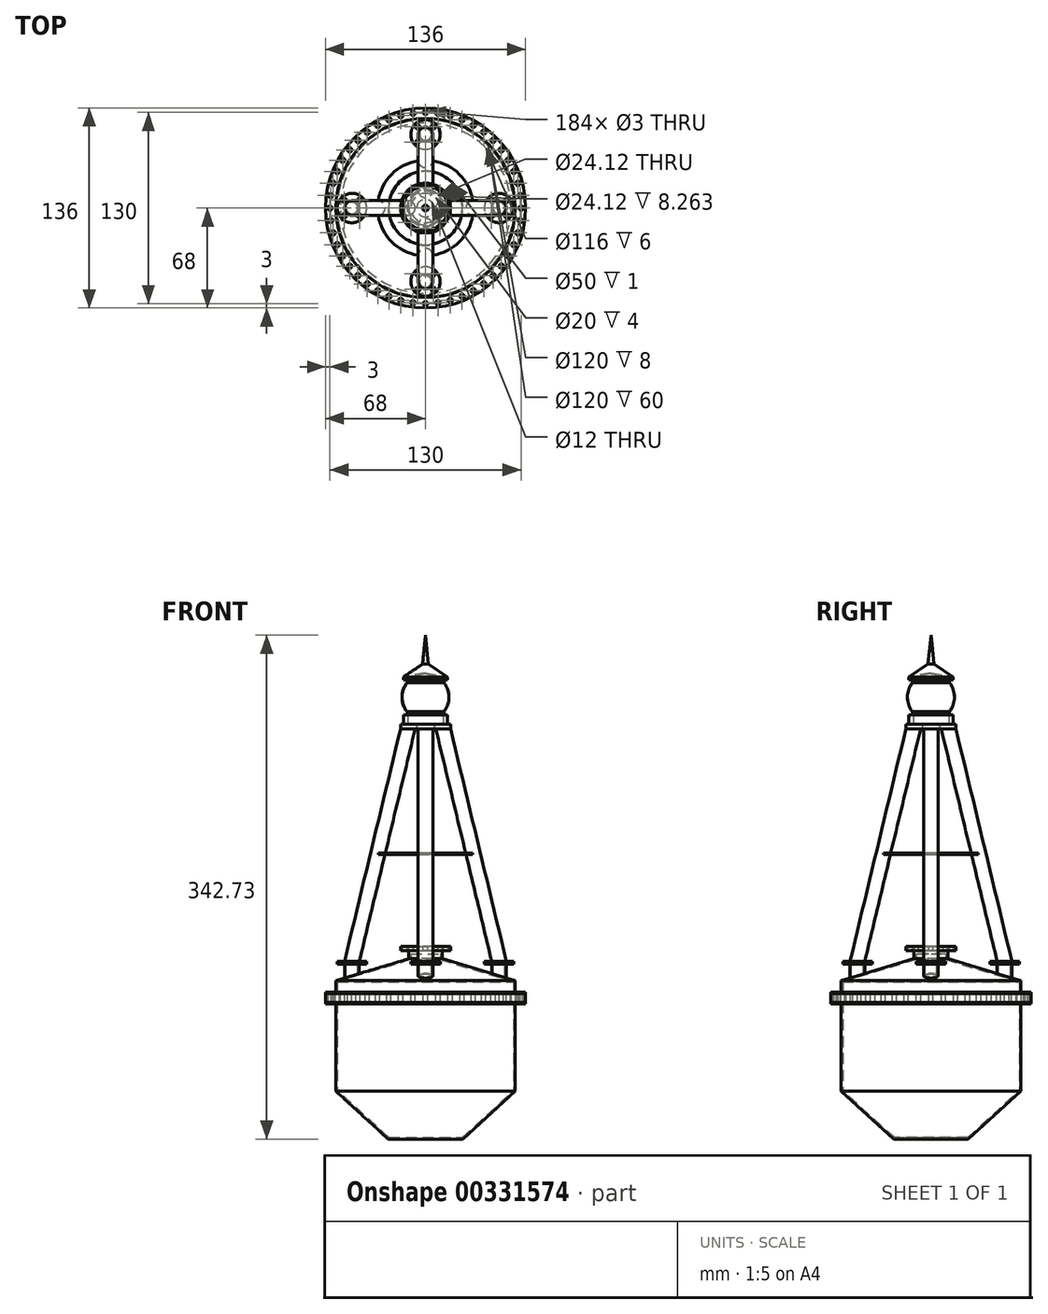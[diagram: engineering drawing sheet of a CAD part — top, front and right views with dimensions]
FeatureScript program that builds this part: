
annotation { "Feature Type Name" : "Feature", "Feature Type Description" : "" }
export const myFeature = defineFeature(function(context is Context, id is Id, definition is map)
    precondition{}
    {
        {
            var Q0;
            Q0=qCreatedBy(makeId("Front.planeOp"),FACE);
            var sketch = newSketch(context, id + "F0", { "sketchPlane" : qUnion([Q0])});
            skLineSegment(sketch, "E0", {"start": v(10, 50) * mm, "end": v(10, 43) * mm});
            skLineSegment(sketch, "E1", {"start": v(10, 43) * mm, "end": v(60, 28) * mm});
            skLineSegment(sketch, "E2", {"start": v(60, 28) * mm, "end": v(60, 20) * mm});
            skLineSegment(sketch, "E3", {"start": v(60, 20) * mm, "end": v(68, 20) * mm});
            skLineSegment(sketch, "E4", {"start": v(68, 14) * mm, "end": v(60, 14) * mm});
            skLineSegment(sketch, "E5", {"start": v(60, 14) * mm, "end": v(60, -46) * mm});
            skLineSegment(sketch, "E6", {"start": v(60, -46) * mm, "end": v(25, -78) * mm});
            skLineSegment(sketch, "E7", {"start": v(25, -78) * mm, "end": v(0, -78) * mm});
            skLineSegment(sketch, "E8.0", {"start": v(61, 21) * mm, "end": v(68, 21) * mm});
            skLineSegment(sketch, "E8.1", {"start": v(17, 49) * mm, "end": v(11.5, 49) * mm});
            skLineSegment(sketch, "E8.2", {"start": v(11.5, 49) * mm, "end": v(11.5, 43.6) * mm});
            skLineSegment(sketch, "E8.3", {"start": v(11.5, 43.6) * mm, "end": v(61, 28.74) * mm});
            skLineSegment(sketch, "E8.4", {"start": v(61, 28.74) * mm, "end": v(61, 21) * mm});
            skLineSegment(sketch, "E9.0", {"start": v(25.39, -79) * mm, "end": v(0, -79) * mm});
            skLineSegment(sketch, "E9.1", {"start": v(61, -46.44) * mm, "end": v(25.39, -79) * mm});
            skLineSegment(sketch, "E9.2", {"start": v(61, 13) * mm, "end": v(61, -46.44) * mm});
            skLineSegment(sketch, "E9.3", {"start": v(68, 13) * mm, "end": v(61, 13) * mm});
            skLineSegment(sketch, "E10", {"start": v(68, 21) * mm, "end": v(68, 20) * mm});
            skLineSegment(sketch, "E11", {"start": v(68, 14) * mm, "end": v(68, 13) * mm});
            skLineSegment(sketch, "E12", {"start": v(0, -78) * mm, "end": v(0, -79) * mm});
            skLineSegment(sketch, "E13.top", {"start": v(60, 14) * mm, "end": v(68, 14) * mm});
            skLineSegment(sketch, "E14", {"start": v(10, 50) * mm, "end": v(17, 50) * mm});
            skLineSegment(sketch, "E15", {"start": v(17, 50) * mm, "end": v(17, 49) * mm});
            skLineSegment(sketch, "E16", {"start": v(0, 0) * mm, "end": v(0, 63.77) * mm, "construction": true});
            skSolve(sketch);
        }
        {
            var Q0;
            Q0=makeQuery(id+"F0.imprint","IMPRINT",FACE,{"disambiguationData":[TD([[makeQuery(id+"F0.imprint","IMPRINT",EDGE,{"derivedFrom":sQuery(id+"F0.wireOp",EDGE,"E0")}),1.0]])]});
            var Q1;
            Q1=makeQuery(id+"F0.imprint","IMPRINT",FACE,{"disambiguationData":[TD([[makeQuery(id+"F0.imprint","IMPRINT",EDGE,{"derivedFrom":sQuery(id+"F0.wireOp",EDGE,"E5")}),1.0]])]});
            var Q2;
            Q2=sQuery(id+"F0.wireOp",EDGE,"E16");
            revolve(context, id + "F1", {"entities" : qUnion([Q0, Q1]), "axis" : qUnion([Q2]), "revolveType" : RevolveType.FULL});
        }
        {
            var Q0;
            Q0=qCreatedBy(makeId("Front.planeOp"),FACE);
            var sketch = newSketch(context, id + "F2", { "sketchPlane" : qUnion([Q0])});
            skLineSegment(sketch, "E17.0", {"start": v(58, 20) * mm, "end": v(68, 20) * mm});
            skLineSegment(sketch, "E17.1", {"start": v(58, 14) * mm, "end": v(68, 14) * mm});
            skLineSegment(sketch, "E18", {"start": v(68, 20) * mm, "end": v(68, 14) * mm});
            skLineSegment(sketch, "E19", {"start": v(58, 20) * mm, "end": v(58, 14) * mm});
            skPoint(sketch, "E20.orphan", {"position": v(-68, 20) * mm});
            skPoint(sketch, "E21.orphan", {"position": v(-68, 14) * mm});
            skLineSegment(sketch, "E22", {"start": v(0, 35.56) * mm, "end": v(0, -17.02) * mm, "construction": true});
            skSolve(sketch);
        }
        {
            var Q0;
            Q0 = qSketchRegion(id + "F2", true);
            var Q1;
            Q1=sQuery(id+"F2.wireOp",EDGE,"E22");
            revolve(context, id + "F3", {"entities" : qUnion([Q0]), "axis" : qUnion([Q1]), "revolveType" : RevolveType.FULL});
        }
        {
            var Q0;
            Q0=makeQuery(id+"F1.opRevolve","SWEPT_FACE",FACE,{"disambiguationData":[OSD([sQuery(id+"F0.wireOp",EDGE,"E14")])]});
            var sketch = newSketch(context, id + "F4", { "sketchPlane" : qUnion([Q0])});
            skCircle(sketch, "E23.0", {"center": v(0, 0) * mm, "radius": 10 * mm});
            skSolve(sketch);
        }
        {
            var Q0;
            Q0 = qSketchRegion(id + "F4", true);
            extrude(context, id + "F5", {"entities" : qUnion([Q0]), "oppositeDirection" : true, "depth" : 3 * mm});
        }
        {
            var Q0;
            Q0=makeQuery(id+"F5.opExtrude","CAP_FACE",FACE,{"disambiguationData":[OSD([sQuery(id+"F4.wireOp",EDGE,"E23.0")])],"isStart":true});
            var sketch = newSketch(context, id + "F6", { "sketchPlane" : qUnion([Q0])});
            skCircle(sketch, "E24.0", {"center": v(0, 0) * mm, "radius": 17 * mm});
            skSolve(sketch);
        }
        {
            var Q0;
            Q0 = qSketchRegion(id + "F6", true);
            extrude(context, id + "F7", {"entities" : qUnion([Q0]), "operationType" : NewBodyOperationType.ADD, "depth" : 2 * mm});
        }
        {
            var Q0;
            Q0=makeQuery(id+"F7.opExtrude","CAP_FACE",FACE,{"disambiguationData":[OSD([sQuery(id+"F6.wireOp",EDGE,"E24.0")])],"isStart":false});
            var sketch = newSketch(context, id + "F8", { "sketchPlane" : qUnion([Q0])});
            skCircle(sketch, "E25", {"center": v(0, 0) * mm, "radius": 14 * mm, "construction": true});
            skCircle(sketch, "E26", {"center": v(0, 14) * mm, "radius": 1.5 * mm});
            skCircle(sketch, "E27.1.0", {"center": v(-9.9, 9.9) * mm, "radius": 1.5 * mm});
            skCircle(sketch, "E27.2.0", {"center": v(-14, 0) * mm, "radius": 1.5 * mm});
            skCircle(sketch, "E27.3.0", {"center": v(-9.9, -9.9) * mm, "radius": 1.5 * mm});
            skCircle(sketch, "E27.4.0", {"center": v(0, -14) * mm, "radius": 1.5 * mm});
            skCircle(sketch, "E27.5.0", {"center": v(9.9, -9.9) * mm, "radius": 1.5 * mm});
            skCircle(sketch, "E27.6.0", {"center": v(14, 0) * mm, "radius": 1.5 * mm});
            skCircle(sketch, "E27.7.0", {"center": v(9.9, 9.9) * mm, "radius": 1.5 * mm});
            skLineSegment(sketch, "E28", {"start": v(-9.9, 9.9) * mm, "end": v(0, 0) * mm, "construction": true});
            skSolve(sketch);
        }
        {
            var Q0;
            Q0 = qSketchRegion(id + "F8", true);
            var Q1;
            Q1=makeQuery(id+"F1.opRevolve","SWEPT_FACE",FACE,{"disambiguationData":[OSD([sQuery(id+"F0.wireOp",EDGE,"E8.1")])]});
            extrude(context, id + "F9", {"entities" : qUnion([Q0]), "operationType" : NewBodyOperationType.REMOVE, "endBound" : BoundingType.UP_TO_SURFACE, "oppositeDirection" : true, "endBoundEntityFace" : qUnion([Q1]), "depth" : 25 * mm});
        }
        {
            var Q0;
            Q0=makeQuery(id+"F1.opRevolve","SWEPT_FACE",FACE,{"disambiguationData":[OSD([sQuery(id+"F0.wireOp",EDGE,"E8.0")])]});
            var sketch = newSketch(context, id + "F10", { "sketchPlane" : qUnion([Q0])});
            skCircle(sketch, "E29", {"center": v(0, 0) * mm, "radius": 65 * mm, "construction": true});
            skCircle(sketch, "E30", {"center": v(-65, 0) * mm, "radius": 1.5 * mm});
            skCircle(sketch, "E31.1.0", {"center": v(-64.44, -8.48) * mm, "radius": 1.5 * mm});
            skCircle(sketch, "E31.2.0", {"center": v(-62.79, -16.82) * mm, "radius": 1.5 * mm});
            skCircle(sketch, "E31.3.0", {"center": v(-60.05, -24.87) * mm, "radius": 1.5 * mm});
            skCircle(sketch, "E31.4.0", {"center": v(-56.3, -32.5) * mm, "radius": 1.5 * mm});
            skCircle(sketch, "E31.5.0", {"center": v(-51.57, -39.57) * mm, "radius": 1.5 * mm});
            skCircle(sketch, "E31.6.0", {"center": v(-45.96, -45.96) * mm, "radius": 1.5 * mm});
            skCircle(sketch, "E31.7.0", {"center": v(-39.57, -51.57) * mm, "radius": 1.5 * mm});
            skCircle(sketch, "E31.8.0", {"center": v(-32.5, -56.3) * mm, "radius": 1.5 * mm});
            skCircle(sketch, "E31.9.0", {"center": v(-24.87, -60.05) * mm, "radius": 1.5 * mm});
            skCircle(sketch, "E31.10.0", {"center": v(-16.82, -62.79) * mm, "radius": 1.5 * mm});
            skCircle(sketch, "E31.11.0", {"center": v(-8.48, -64.44) * mm, "radius": 1.5 * mm});
            skCircle(sketch, "E31.12.0", {"center": v(0, -65) * mm, "radius": 1.5 * mm});
            skCircle(sketch, "E31.13.0", {"center": v(8.48, -64.44) * mm, "radius": 1.5 * mm});
            skCircle(sketch, "E31.14.0", {"center": v(16.82, -62.79) * mm, "radius": 1.5 * mm});
            skCircle(sketch, "E31.15.0", {"center": v(24.87, -60.05) * mm, "radius": 1.5 * mm});
            skCircle(sketch, "E31.16.0", {"center": v(32.5, -56.3) * mm, "radius": 1.5 * mm});
            skCircle(sketch, "E31.17.0", {"center": v(39.57, -51.57) * mm, "radius": 1.5 * mm});
            skCircle(sketch, "E31.18.0", {"center": v(45.96, -45.96) * mm, "radius": 1.5 * mm});
            skCircle(sketch, "E31.19.0", {"center": v(51.57, -39.57) * mm, "radius": 1.5 * mm});
            skCircle(sketch, "E31.20.0", {"center": v(56.3, -32.5) * mm, "radius": 1.5 * mm});
            skCircle(sketch, "E31.21.0", {"center": v(60.05, -24.87) * mm, "radius": 1.5 * mm});
            skCircle(sketch, "E31.22.0", {"center": v(62.79, -16.82) * mm, "radius": 1.5 * mm});
            skCircle(sketch, "E31.23.0", {"center": v(64.44, -8.48) * mm, "radius": 1.5 * mm});
            skCircle(sketch, "E31.24.0", {"center": v(65, 0) * mm, "radius": 1.5 * mm});
            skCircle(sketch, "E31.25.0", {"center": v(64.44, 8.48) * mm, "radius": 1.5 * mm});
            skCircle(sketch, "E31.26.0", {"center": v(62.79, 16.82) * mm, "radius": 1.5 * mm});
            skCircle(sketch, "E31.27.0", {"center": v(60.05, 24.87) * mm, "radius": 1.5 * mm});
            skCircle(sketch, "E31.28.0", {"center": v(56.3, 32.5) * mm, "radius": 1.5 * mm});
            skCircle(sketch, "E31.29.0", {"center": v(51.57, 39.57) * mm, "radius": 1.5 * mm});
            skCircle(sketch, "E31.30.0", {"center": v(45.96, 45.96) * mm, "radius": 1.5 * mm});
            skCircle(sketch, "E31.31.0", {"center": v(39.57, 51.57) * mm, "radius": 1.5 * mm});
            skCircle(sketch, "E31.32.0", {"center": v(32.5, 56.3) * mm, "radius": 1.5 * mm});
            skCircle(sketch, "E31.33.0", {"center": v(24.87, 60.05) * mm, "radius": 1.5 * mm});
            skCircle(sketch, "E31.34.0", {"center": v(16.82, 62.79) * mm, "radius": 1.5 * mm});
            skCircle(sketch, "E31.35.0", {"center": v(8.48, 64.44) * mm, "radius": 1.5 * mm});
            skCircle(sketch, "E31.36.0", {"center": v(0, 65) * mm, "radius": 1.5 * mm});
            skCircle(sketch, "E31.37.0", {"center": v(-8.48, 64.44) * mm, "radius": 1.5 * mm});
            skCircle(sketch, "E31.38.0", {"center": v(-16.82, 62.79) * mm, "radius": 1.5 * mm});
            skCircle(sketch, "E31.39.0", {"center": v(-24.87, 60.05) * mm, "radius": 1.5 * mm});
            skCircle(sketch, "E31.40.0", {"center": v(-32.5, 56.3) * mm, "radius": 1.5 * mm});
            skCircle(sketch, "E31.41.0", {"center": v(-39.57, 51.57) * mm, "radius": 1.5 * mm});
            skCircle(sketch, "E31.42.0", {"center": v(-45.96, 45.96) * mm, "radius": 1.5 * mm});
            skCircle(sketch, "E31.43.0", {"center": v(-51.57, 39.57) * mm, "radius": 1.5 * mm});
            skCircle(sketch, "E31.44.0", {"center": v(-56.3, 32.5) * mm, "radius": 1.5 * mm});
            skCircle(sketch, "E31.45.0", {"center": v(-60.05, 24.87) * mm, "radius": 1.5 * mm});
            skCircle(sketch, "E31.46.0", {"center": v(-62.79, 16.82) * mm, "radius": 1.5 * mm});
            skCircle(sketch, "E31.47.0", {"center": v(-64.44, 8.48) * mm, "radius": 1.5 * mm});
            skLineSegment(sketch, "E32", {"start": v(-64.44, -8.48) * mm, "end": v(0, 0) * mm, "construction": true});
            skSolve(sketch);
        }
        {
            var Q0;
            Q0 = qSketchRegion(id + "F10", true);
            var Q1;
            Q1=makeQuery(id+"F1.opRevolve","SWEPT_FACE",FACE,{"disambiguationData":[OSD([sQuery(id+"F0.wireOp",EDGE,"E9.3")])]});
            var Q2;
            Q2=makeQuery(id+"F1.opRevolve","SWEPT_FACE",FACE,{"disambiguationData":[OSD([sQuery(id+"F0.wireOp",EDGE,"E9.3")])]});
            extrude(context, id + "F11", {"entities" : qUnion([Q0, Q1]), "operationType" : NewBodyOperationType.REMOVE, "oppositeDirection" : true, "endBoundEntityFace" : qUnion([Q2]), "depth" : 25 * mm});
        }
        {
            var Q0;
            Q0=qCreatedBy(makeId("Top.planeOp"),FACE);
            cPlane(context, id + "F12", {"entities" : qUnion([Q0]), "cplaneType" : CPlaneType.OFFSET, "offset" : 40 * mm, "width" : 150 * mm, "height" : 150 * mm});
        }
        {
            var Q0;
            Q0=qCreatedBy(id+"F12.planeOp",FACE);
            var sketch = newSketch(context, id + "F13", { "sketchPlane" : qUnion([Q0])});
            skCircle(sketch, "E33", {"center": v(0, 0) * mm, "radius": 50 * mm, "construction": true});
            skCircle(sketch, "E34", {"center": v(0, 50) * mm, "radius": 5 * mm});
            skCircle(sketch, "E35.0", {"center": v(0, 50) * mm, "radius": 4 * mm});
            skCircle(sketch, "E36.1.0", {"center": v(-50, 0) * mm, "radius": 5 * mm});
            skCircle(sketch, "E36.1.1", {"center": v(-50, 0) * mm, "radius": 4 * mm});
            skCircle(sketch, "E36.2.0", {"center": v(0, -50) * mm, "radius": 5 * mm});
            skCircle(sketch, "E36.2.1", {"center": v(0, -50) * mm, "radius": 4 * mm});
            skCircle(sketch, "E36.3.0", {"center": v(50, 0) * mm, "radius": 5 * mm});
            skCircle(sketch, "E36.3.1", {"center": v(50, 0) * mm, "radius": 4 * mm});
            skLineSegment(sketch, "E37", {"start": v(-50, 0) * mm, "end": v(0, 0) * mm, "construction": true});
            skSolve(sketch);
        }
        {
            var Q0;
            Q0 = qSketchRegion(id + "F13", true);
            extrude(context, id + "F14", {"entities" : qUnion([Q0]), "operationType" : NewBodyOperationType.ADD, "endBound" : BoundingType.UP_TO_NEXT, "oppositeDirection" : true, "depth" : 25 * mm});
        }
        {
            var Q0;
            Q0=qCreatedBy(id+"F12.planeOp",FACE);
            var sketch = newSketch(context, id + "F15", { "sketchPlane" : qUnion([Q0])});
            skCircle(sketch, "E38.0", {"center": v(0, 50) * mm, "radius": 4 * mm});
            skCircle(sketch, "E39", {"center": v(0, 50) * mm, "radius": 10 * mm});
            skCircle(sketch, "E40.1.0", {"center": v(-50, 0) * mm, "radius": 10 * mm});
            skCircle(sketch, "E40.2.0", {"center": v(0, -50) * mm, "radius": 10 * mm});
            skCircle(sketch, "E40.3.0", {"center": v(50, 0) * mm, "radius": 10 * mm});
            skPoint(sketch, "E40.center", {"position": v(0, 0) * mm});
            skCircle(sketch, "E41", {"center": v(0, 50) * mm, "radius": 7.5 * mm, "construction": true});
            skCircle(sketch, "E42", {"center": v(5.3, 55.3) * mm, "radius": 1.5 * mm});
            skLineSegment(sketch, "E43", {"start": v(5.3, 55.3) * mm, "end": v(0, 50) * mm, "construction": true});
            skLineSegment(sketch, "E44", {"start": v(0, 50) * mm, "end": v(0, 58.96) * mm, "construction": true});
            skCircle(sketch, "E45.1.0", {"center": v(-5.3, 55.3) * mm, "radius": 1.5 * mm});
            skCircle(sketch, "E45.2.0", {"center": v(-5.3, 44.7) * mm, "radius": 1.5 * mm});
            skCircle(sketch, "E45.3.0", {"center": v(5.3, 44.7) * mm, "radius": 1.5 * mm});
            skCircle(sketch, "E46.1.0", {"center": v(-55.3, -5.3) * mm, "radius": 1.5 * mm});
            skCircle(sketch, "E46.1.1", {"center": v(-55.3, 5.3) * mm, "radius": 1.5 * mm});
            skCircle(sketch, "E46.1.2", {"center": v(-44.7, 5.3) * mm, "radius": 1.5 * mm});
            skCircle(sketch, "E46.1.3", {"center": v(-44.7, -5.3) * mm, "radius": 1.5 * mm});
            skCircle(sketch, "E46.2.0", {"center": v(5.3, -55.3) * mm, "radius": 1.5 * mm});
            skCircle(sketch, "E46.2.1", {"center": v(-5.3, -55.3) * mm, "radius": 1.5 * mm});
            skCircle(sketch, "E46.2.2", {"center": v(-5.3, -44.7) * mm, "radius": 1.5 * mm});
            skCircle(sketch, "E46.2.3", {"center": v(5.3, -44.7) * mm, "radius": 1.5 * mm});
            skCircle(sketch, "E46.3.0", {"center": v(55.3, 5.3) * mm, "radius": 1.5 * mm});
            skCircle(sketch, "E46.3.1", {"center": v(55.3, -5.3) * mm, "radius": 1.5 * mm});
            skCircle(sketch, "E46.3.2", {"center": v(44.7, -5.3) * mm, "radius": 1.5 * mm});
            skCircle(sketch, "E46.3.3", {"center": v(44.7, 5.3) * mm, "radius": 1.5 * mm});
            skCircle(sketch, "E47", {"center": v(-50, 0) * mm, "radius": 7.5 * mm, "construction": true});
            skSolve(sketch);
        }
        {
            var Q0;
            Q0 = qSketchRegion(id + "F15", true);
            var Q1;
            Q1=makeQuery(id+"F15.imprint","IMPRINT",FACE,{"disambiguationData":[TD([[makeQuery(id+"F15.imprint","IMPRINT",EDGE,{"derivedFrom":sQuery(id+"F15.wireOp",EDGE,"E38.0")}),1.0]])]});
            extrude(context, id + "F16", {"entities" : qUnion([Q0, Q1]), "operationType" : NewBodyOperationType.ADD, "depth" : 1 * mm});
        }
        {
            var Q0;
            Q0=makeQuery(id+"F16.opExtrude","CAP_FACE",FACE,{"disambiguationData":[OSD([sQuery(id+"F15.wireOp",EDGE,"E39"),sQuery(id+"F15.wireOp",EDGE,"E42"),sQuery(id+"F15.wireOp",EDGE,"E45.1.0"),sQuery(id+"F15.wireOp",EDGE,"E45.2.0"),sQuery(id+"F15.wireOp",EDGE,"E45.3.0")])],"isStart":false});
            var sketch = newSketch(context, id + "F17", { "sketchPlane" : qUnion([Q0])});
            skCircle(sketch, "E48.0", {"center": v(0, 50) * mm, "radius": 10 * mm});
            skCircle(sketch, "E48.1", {"center": v(-5.3, 44.7) * mm, "radius": 1.5 * mm});
            skCircle(sketch, "E48.2", {"center": v(-5.3, 55.3) * mm, "radius": 1.5 * mm});
            skCircle(sketch, "E48.3", {"center": v(5.3, 55.3) * mm, "radius": 1.5 * mm});
            skCircle(sketch, "E48.4", {"center": v(5.3, 44.7) * mm, "radius": 1.5 * mm});
            skCircle(sketch, "E49.0", {"center": v(-50, 0) * mm, "radius": 10 * mm});
            skCircle(sketch, "E49.1", {"center": v(-44.7, 5.3) * mm, "radius": 1.5 * mm});
            skCircle(sketch, "E49.2", {"center": v(-55.3, 5.3) * mm, "radius": 1.5 * mm});
            skCircle(sketch, "E50.0", {"center": v(-55.3, -5.3) * mm, "radius": 1.5 * mm});
            skCircle(sketch, "E50.1", {"center": v(-44.7, -5.3) * mm, "radius": 1.5 * mm});
            skCircle(sketch, "E51.0", {"center": v(50, 0) * mm, "radius": 10 * mm});
            skCircle(sketch, "E51.1", {"center": v(55.3, 5.3) * mm, "radius": 1.5 * mm});
            skCircle(sketch, "E51.2", {"center": v(44.7, 5.3) * mm, "radius": 1.5 * mm});
            skCircle(sketch, "E51.3", {"center": v(44.7, -5.3) * mm, "radius": 1.5 * mm});
            skCircle(sketch, "E51.4", {"center": v(55.3, -5.3) * mm, "radius": 1.5 * mm});
            skCircle(sketch, "E52.0", {"center": v(5.3, -44.7) * mm, "radius": 1.5 * mm});
            skCircle(sketch, "E52.1", {"center": v(-5.3, -44.7) * mm, "radius": 1.5 * mm});
            skCircle(sketch, "E52.2", {"center": v(-5.3, -55.3) * mm, "radius": 1.5 * mm});
            skCircle(sketch, "E52.3", {"center": v(5.3, -55.3) * mm, "radius": 1.5 * mm});
            skCircle(sketch, "E52.4", {"center": v(0, -50) * mm, "radius": 10 * mm});
            skSolve(sketch);
        }
        {
            var Q0;
            Q0 = qSketchRegion(id + "F17", true);
            extrude(context, id + "F18", {"entities" : qUnion([Q0]), "depth" : 1 * mm});
        }
        {
            var Q0;
            Q0=makeQuery(id+"F18.opExtrude","CAP_FACE",FACE,{"disambiguationData":[OSD([sQuery(id+"F17.wireOp",EDGE,"E49.0"),sQuery(id+"F17.wireOp",EDGE,"E49.1"),sQuery(id+"F17.wireOp",EDGE,"E49.2"),sQuery(id+"F17.wireOp",EDGE,"E50.0"),sQuery(id+"F17.wireOp",EDGE,"E50.1")])],"isStart":false});
            var sketch = newSketch(context, id + "F19", { "sketchPlane" : qUnion([Q0])});
            skCircle(sketch, "E53.0", {"center": v(0, 50) * mm, "radius": 5 * mm});
            skCircle(sketch, "E54.0", {"center": v(50, 0) * mm, "radius": 5 * mm});
            skCircle(sketch, "E54.3", {"center": v(-50, 0) * mm, "radius": 5 * mm});
            skCircle(sketch, "E54.4", {"center": v(0, -50) * mm, "radius": 5 * mm});
            skSolve(sketch);
        }
        {
            var Q0;
            Q0=qCreatedBy(makeId("Top.planeOp"),FACE);
            cPlane(context, id + "F20", {"entities" : qUnion([Q0]), "cplaneType" : CPlaneType.OFFSET, "offset" : 200 * mm, "width" : 150 * mm, "height" : 150 * mm});
        }
        {
            var Q0;
            Q0=qCreatedBy(id+"F20.planeOp",FACE);
            var sketch = newSketch(context, id + "F21", { "sketchPlane" : qUnion([Q0])});
            skCircle(sketch, "E55.0", {"center": v(0, 0) * mm, "radius": 17 * mm});
            skCircle(sketch, "E56", {"center": v(0, 12) * mm, "radius": 5 * mm});
            skCircle(sketch, "E57", {"center": v(0, 0) * mm, "radius": 12 * mm, "construction": true});
            skCircle(sketch, "E58.1.0", {"center": v(-12, 0) * mm, "radius": 5 * mm});
            skCircle(sketch, "E58.2.0", {"center": v(0, -12) * mm, "radius": 5 * mm});
            skCircle(sketch, "E58.3.0", {"center": v(12, 0) * mm, "radius": 5 * mm});
            skLineSegment(sketch, "E59", {"start": v(-12, 0) * mm, "end": v(0, 0) * mm, "construction": true});
            skLineSegment(sketch, "E60", {"start": v(0, 12) * mm, "end": v(0, 0) * mm, "construction": true});
            skSolve(sketch);
        }
        {
            var Q0;
            Q0=qCreatedBy(makeId("Front.planeOp"),FACE);
            var sketch = newSketch(context, id + "F22", { "sketchPlane" : qUnion([Q0])});
            skPoint(sketch, "E61.0", {"position": v(-50, 42) * mm});
            skPoint(sketch, "E62.0", {"position": v(-12, 200) * mm});
            skLineSegment(sketch, "E63", {"start": v(-50, 42) * mm, "end": v(-12, 200) * mm});
            skPoint(sketch, "E64.0", {"position": v(12, 200) * mm});
            skPoint(sketch, "E65.0", {"position": v(50, 42) * mm});
            skSolve(sketch);
        }
        {
            var Q0;
            Q0=makeQuery(id+"F19.imprint","IMPRINT",FACE,{"disambiguationData":[TD([[makeQuery(id+"F19.imprint","IMPRINT",EDGE,{"derivedFrom":sQuery(id+"F19.wireOp",EDGE,"E54.3")}),1.0]])]});
            var Q1;
            Q1=sQuery(id+"F22.wireOp",EDGE,"E63");
            sweep(context, id + "F23", {"operationType" : NewBodyOperationType.ADD, "profiles" : qUnion([Q0]), "path" : qUnion([Q1])});
        }
        {
            var Q0;
            Q0=makeQuery(id+"F18.opExtrude","CAP_FACE",FACE,{"disambiguationData":[OSD([sQuery(id+"F17.wireOp",EDGE,"E51.0"),sQuery(id+"F17.wireOp",EDGE,"E51.1"),sQuery(id+"F17.wireOp",EDGE,"E51.2"),sQuery(id+"F17.wireOp",EDGE,"E51.3"),sQuery(id+"F17.wireOp",EDGE,"E51.4")])],"isStart":false});
            var sketch = newSketch(context, id + "F24", { "sketchPlane" : qUnion([Q0])});
            skCircle(sketch, "E66.0", {"center": v(50, 0) * mm, "radius": 10 * mm});
            skCircle(sketch, "E67.0", {"center": v(50, 0) * mm, "radius": 5 * mm});
            skSolve(sketch);
        }
        {
            var Q0;
            Q0=qCreatedBy(makeId("Front.planeOp"),FACE);
            var sketch = newSketch(context, id + "F25", { "sketchPlane" : qUnion([Q0])});
            skPoint(sketch, "E68.0", {"position": v(12, 200) * mm});
            skPoint(sketch, "E69.0", {"position": v(50, 42) * mm});
            skLineSegment(sketch, "E70", {"start": v(50, 42) * mm, "end": v(12, 200) * mm});
            skSolve(sketch);
        }
        {
            var Q0;
            Q0=makeQuery(id+"F24.imprint","IMPRINT",FACE,{"disambiguationData":[TD([[makeQuery(id+"F24.imprint","IMPRINT",EDGE,{"derivedFrom":sQuery(id+"F24.wireOp",EDGE,"E67.0")}),1.0]])]});
            var Q1;
            Q1=sQuery(id+"F25.wireOp",EDGE,"E70");
            sweep(context, id + "F26", {"operationType" : NewBodyOperationType.ADD, "profiles" : qUnion([Q0]), "path" : qUnion([Q1])});
        }
        {
            var Q0;
            Q0=makeQuery(id+"F18.opExtrude","CAP_FACE",FACE,{"disambiguationData":[OSD([sQuery(id+"F17.wireOp",EDGE,"E48.0"),sQuery(id+"F17.wireOp",EDGE,"E48.1"),sQuery(id+"F17.wireOp",EDGE,"E48.2"),sQuery(id+"F17.wireOp",EDGE,"E48.3"),sQuery(id+"F17.wireOp",EDGE,"E48.4")])],"isStart":false});
            var sketch = newSketch(context, id + "F27", { "sketchPlane" : qUnion([Q0])});
            skCircle(sketch, "E71.0", {"center": v(0, 50) * mm, "radius": 5 * mm});
            skSolve(sketch);
        }
        {
            var Q0;
            Q0=qCreatedBy(makeId("Right.planeOp"),FACE);
            var sketch = newSketch(context, id + "F28", { "sketchPlane" : qUnion([Q0])});
            skPoint(sketch, "E72.0", {"position": v(50, 42) * mm});
            skPoint(sketch, "E73.0", {"position": v(12, 200) * mm});
            skLineSegment(sketch, "E74", {"start": v(12, 200) * mm, "end": v(50, 42) * mm});
            skSolve(sketch);
        }
        {
            var Q0;
            Q0=makeQuery(id+"F27.imprint","IMPRINT",FACE,{"disambiguationData":[TD([[makeQuery(id+"F27.imprint","IMPRINT",EDGE,{"derivedFrom":sQuery(id+"F27.wireOp",EDGE,"E71.0")}),1.0]])]});
            var Q1;
            Q1=sQuery(id+"F28.wireOp",EDGE,"E74");
            sweep(context, id + "F29", {"operationType" : NewBodyOperationType.ADD, "profiles" : qUnion([Q0]), "path" : qUnion([Q1])});
        }
        {
            var Q0;
            Q0=makeQuery(id+"F18.opExtrude","CAP_FACE",FACE,{"disambiguationData":[OSD([sQuery(id+"F17.wireOp",EDGE,"E52.0"),sQuery(id+"F17.wireOp",EDGE,"E52.1"),sQuery(id+"F17.wireOp",EDGE,"E52.2"),sQuery(id+"F17.wireOp",EDGE,"E52.3"),sQuery(id+"F17.wireOp",EDGE,"E52.4")])],"isStart":false});
            var sketch = newSketch(context, id + "F30", { "sketchPlane" : qUnion([Q0])});
            skCircle(sketch, "E75.0", {"center": v(0, -50) * mm, "radius": 5 * mm});
            skSolve(sketch);
        }
        {
            var Q0;
            Q0=qCreatedBy(makeId("Right.planeOp"),FACE);
            var sketch = newSketch(context, id + "F31", { "sketchPlane" : qUnion([Q0])});
            skPoint(sketch, "E76.0", {"position": v(-50, 42) * mm});
            skPoint(sketch, "E77.0", {"position": v(-12, 200) * mm});
            skLineSegment(sketch, "E78", {"start": v(-12, 200) * mm, "end": v(-50, 42) * mm});
            skSolve(sketch);
        }
        {
            var Q0;
            Q0=makeQuery(id+"F30.imprint","IMPRINT",FACE,{"disambiguationData":[TD([[makeQuery(id+"F30.imprint","IMPRINT",EDGE,{"derivedFrom":sQuery(id+"F30.wireOp",EDGE,"E75.0")}),1.0]])]});
            var Q1;
            Q1=sQuery(id+"F31.wireOp",EDGE,"E78");
            sweep(context, id + "F32", {"operationType" : NewBodyOperationType.ADD, "profiles" : qUnion([Q0]), "path" : qUnion([Q1])});
        }
        {
            var Q0;
            Q0=qCreatedBy(id+"F20.planeOp",FACE);
            var sketch = newSketch(context, id + "F33", { "sketchPlane" : qUnion([Q0])});
            skCircle(sketch, "E79.0", {"center": v(0, 0) * mm, "radius": 17 * mm});
            skCircle(sketch, "E80", {"center": v(0, 0) * mm, "radius": 6 * mm});
            skSolve(sketch);
        }
        {
            var Q0;
            Q0 = qSketchRegion(id + "F33", true);
            extrude(context, id + "F34", {"entities" : qUnion([Q0]), "depth" : 3 * mm});
        }
        {
            var Q0;
            Q0=qCreatedBy(id+"F12.planeOp",FACE);
            cPlane(context, id + "F35", {"entities" : qUnion([Q0]), "cplaneType" : CPlaneType.OFFSET, "offset" : 75 * mm, "width" : 150 * mm, "height" : 150 * mm});
        }
        {
            var Q0;
            Q0=qCreatedBy(id+"F35.planeOp",FACE);
            var sketch = newSketch(context, id + "F36", { "sketchPlane" : qUnion([Q0])});
            skArc(sketch, "E81", {"start": v(-32.11, -5.01) * mm, "mid": v(-22.98, -22.98) * mm, "end": v(-5.01, -32.11) * mm});
            skLineSegment(sketch, "E82", {"start": v(0, 0) * mm, "end": v(-27.47, 0) * mm, "construction": true});
            skArc(sketch, "E83", {"start": v(-32.11, -5.01) * mm, "mid": v(-27.47, 0) * mm, "end": v(-32.11, 5.01) * mm});
            skLineSegment(sketch, "E84.trimOffspring", {"start": v(-32.5, 0) * mm, "end": v(-42.95, 0) * mm, "construction": true});
            skArc(sketch, "E85.1.0", {"start": v(5.01, -32.11) * mm, "mid": v(0, -27.47) * mm, "end": v(-5.01, -32.11) * mm});
            skArc(sketch, "E85.2.0", {"start": v(32.11, 5.01) * mm, "mid": v(27.47, 0) * mm, "end": v(32.11, -5.01) * mm});
            skArc(sketch, "E85.3.0", {"start": v(-5.01, 32.11) * mm, "mid": v(0, 27.47) * mm, "end": v(5.01, 32.11) * mm});
            skLineSegment(sketch, "E86", {"start": v(0, 0) * mm, "end": v(0, -36.84) * mm, "construction": true});
            skArc(sketch, "E87.trimOffspring", {"start": v(-5.01, 32.11) * mm, "mid": v(-22.98, 22.98) * mm, "end": v(-32.11, 5.01) * mm});
            skArc(sketch, "E88.trimOffspring", {"start": v(32.11, 5.01) * mm, "mid": v(22.98, 22.98) * mm, "end": v(5.01, 32.11) * mm});
            skArc(sketch, "E89.trimOffspring", {"start": v(5.01, -32.11) * mm, "mid": v(22.98, -22.98) * mm, "end": v(32.11, -5.01) * mm});
            skCircle(sketch, "E90", {"center": v(0, 0) * mm, "radius": 25 * mm});
            skSolve(sketch);
        }
        {
            var Q0;
            Q0 = qSketchRegion(id + "F36", true);
            extrude(context, id + "F37", {"entities" : qUnion([Q0]), "depth" : 1 * mm, "symmetric" : true});
        }
        {
            var Q0;
            Q0=qCreatedBy(makeId("Front.planeOp"),FACE);
            var sketch = newSketch(context, id + "F38", { "sketchPlane" : qUnion([Q0])});
            skLineSegment(sketch, "E91", {"start": v(0, 203.58) * mm, "end": v(0, 247.8) * mm, "construction": true});
            skLineSegment(sketch, "E92", {"start": v(0, 238) * mm, "end": v(15, 235.36) * mm});
            skLineSegment(sketch, "E93", {"start": v(15, 235.36) * mm, "end": v(15, 233.36) * mm});
            skLineSegment(sketch, "E94", {"start": v(15, 233.36) * mm, "end": v(12.56, 233.36) * mm});
            skLineSegment(sketch, "E95", {"start": v(12.56, 233.36) * mm, "end": v(12.56, 231.41) * mm});
            skLineSegment(sketch, "E96", {"start": v(12.56, 211.59) * mm, "end": v(12.56, 209.5) * mm});
            skLineSegment(sketch, "E97", {"start": v(12.56, 209.5) * mm, "end": v(15, 209.5) * mm});
            skLineSegment(sketch, "E98", {"start": v(15, 209.5) * mm, "end": v(15, 203) * mm});
            skLineSegment(sketch, "E99", {"start": v(15, 203) * mm, "end": v(0, 203) * mm});
            skArc(sketch, "E100.trimOffspring", {"start": v(12.56, 211.59) * mm, "mid": v(16, 221.5) * mm, "end": v(12.56, 231.41) * mm});
            skLineSegment(sketch, "E101.0", {"start": v(12.06, 203.5) * mm, "end": v(0, 203.5) * mm});
            skLineSegment(sketch, "E101.1", {"start": v(0, 237.5) * mm, "end": v(12.06, 235.37) * mm});
            skLineSegment(sketch, "E101.2", {"start": v(12.06, 235.37) * mm, "end": v(12.06, 231.24) * mm});
            skArc(sketch, "E101.3", {"start": v(12.06, 211.76) * mm, "mid": v(15.5, 221.5) * mm, "end": v(12.06, 231.24) * mm});
            skLineSegment(sketch, "E101.4", {"start": v(12.06, 211.76) * mm, "end": v(12.06, 203.5) * mm});
            skLineSegment(sketch, "E102", {"start": v(0, 238) * mm, "end": v(0, 237.5) * mm});
            skLineSegment(sketch, "E103", {"start": v(0, 203) * mm, "end": v(0, 203.5) * mm});
            skSolve(sketch);
        }
        {
            var Q0;
            Q0 = qSketchRegion(id + "F38", true);
            var Q1;
            Q1=sQuery(id+"F38.wireOp",EDGE,"E91");
            revolve(context, id + "F39", {"entities" : qUnion([Q0]), "axis" : qUnion([Q1]), "revolveType" : RevolveType.FULL});
        }
        {
            var Q0;
            Q0=qCreatedBy(makeId("Front.planeOp"),FACE);
            var sketch = newSketch(context, id + "F40", { "sketchPlane" : qUnion([Q0])});
            skPoint(sketch, "E104.0", {"position": v(0, 238) * mm});
            skLineSegment(sketch, "E104.1", {"start": v(15, 235.36) * mm, "end": v(-15, 235.36) * mm});
            skLineSegment(sketch, "E105", {"start": v(0, 238) * mm, "end": v(0, 263.73) * mm});
            skLineSegment(sketch, "E106", {"start": v(15, 235.36) * mm, "end": v(0, 238) * mm});
            skLineSegment(sketch, "E107", {"start": v(0, 263.73) * mm, "end": v(2, 244) * mm});
            skLineSegment(sketch, "E108", {"start": v(2, 244) * mm, "end": v(15, 235.36) * mm});
            skSolve(sketch);
        }
        {
            var Q0;
            Q0 = qSketchRegion(id + "F40", true);
            var Q1;
            Q1=sQuery(id+"F40.wireOp",EDGE,"E105");
            revolve(context, id + "F41", {"entities" : qUnion([Q0]), "axis" : qUnion([Q1]), "revolveType" : RevolveType.FULL});
        }
    });
